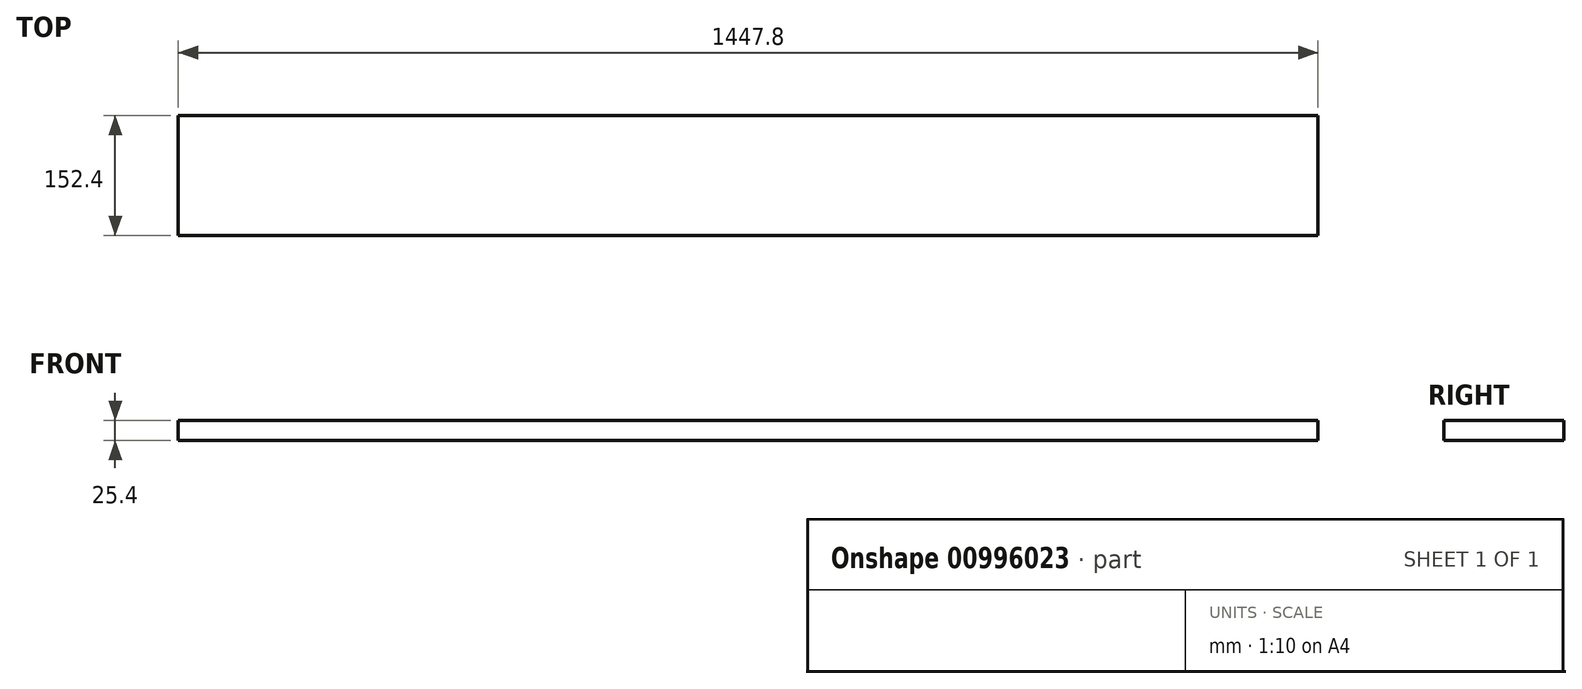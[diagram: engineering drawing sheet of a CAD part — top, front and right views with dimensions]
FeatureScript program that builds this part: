
annotation { "Feature Type Name" : "Feature", "Feature Type Description" : "" }
export const myFeature = defineFeature(function(context is Context, id is Id, definition is map)
    precondition{}
    {
        {
            var Q0;
            Q0=qCreatedBy(makeId("Top.planeOp"),FACE);
            var sketch = newSketch(context, id + "F0", { "sketchPlane" : qUnion([Q0])});
            skLineSegment(sketch, "E0.bottom", {"start": v(0, 0) * mm, "end": v(1447.8, 0) * mm});
            skLineSegment(sketch, "E0.top", {"start": v(0, 152.4) * mm, "end": v(1447.8, 152.4) * mm});
            skLineSegment(sketch, "E0.left", {"start": v(0, 0) * mm, "end": v(0, 152.4) * mm});
            skLineSegment(sketch, "E0.right", {"start": v(1447.8, 0) * mm, "end": v(1447.8, 152.4) * mm});
            skSolve(sketch);
        }
        {
            var Q0;
            Q0 = qSketchRegion(id + "F0", true);
            extrude(context, id + "F1", {"entities" : qUnion([Q0]), "depth" : 25.4 * mm, "offsetDistance" : 25.4 * mm});
        }
    });
